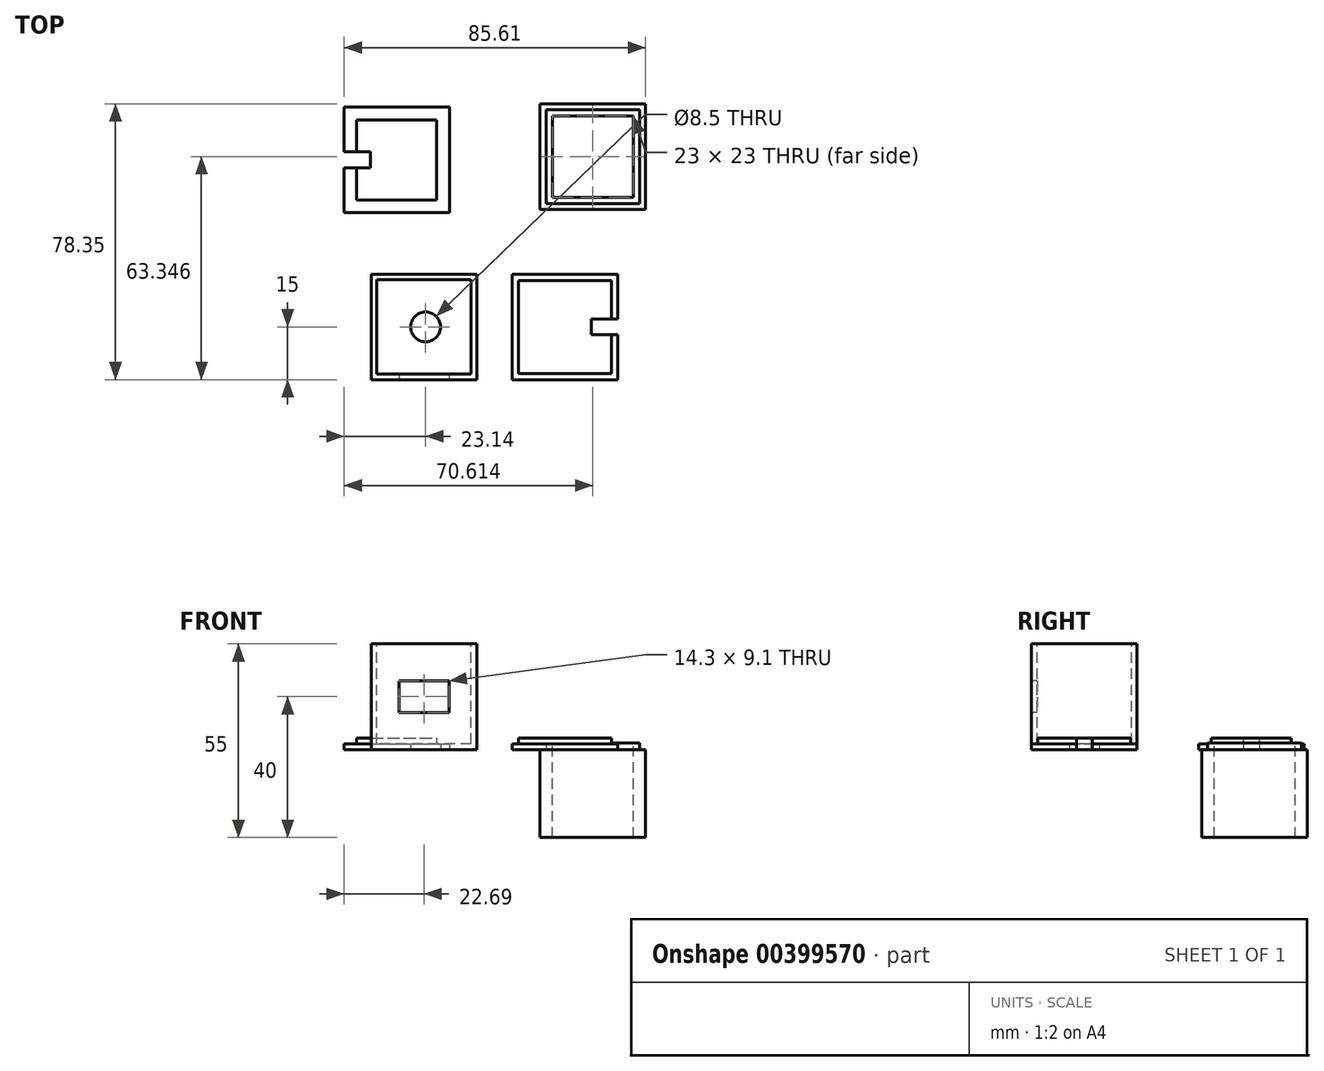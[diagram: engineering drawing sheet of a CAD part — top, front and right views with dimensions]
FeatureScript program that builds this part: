
annotation { "Feature Type Name" : "Feature", "Feature Type Description" : "" }
export const myFeature = defineFeature(function(context is Context, id is Id, definition is map)
    precondition{}
    {
        {
            var Q0;
            Q0=qCreatedBy(makeId("Front.planeOp"),FACE);
            var sketch = newSketch(context, id + "F0", { "sketchPlane" : qUnion([Q0])});
            skLineSegment(sketch, "E0.bottom", {"start": v(0, 0) * mm, "end": v(-30, 0) * mm});
            skLineSegment(sketch, "E0.top", {"start": v(0, 30) * mm, "end": v(-30, 30) * mm});
            skLineSegment(sketch, "E0.left", {"start": v(0, 0) * mm, "end": v(0, 30) * mm});
            skLineSegment(sketch, "E0.right", {"start": v(-30, 0) * mm, "end": v(-30, 30) * mm});
            skSolve(sketch);
        }
        {
            var Q0;
            Q0=makeQuery(id+"F0.imprint","IMPRINT",FACE,{"disambiguationData":[TD([[makeQuery(id+"F0.imprint","IMPRINT",EDGE,{"derivedFrom":sQuery(id+"F0.wireOp",EDGE,"E0.bottom")}),-1.0]])]});
            extrude(context, id + "F1", {"entities" : qUnion([Q0]), "depth" : 30 * mm});
        }
        {
            var Q0;
            Q0=makeQuery(id+"F1.opExtrude","SWEPT_FACE",FACE,{"disambiguationData":[OSD([sQuery(id+"F0.wireOp",EDGE,"E0.top")])]});
            shell(context, id + "F2", {"entities" : qUnion([Q0]), "thickness" : 1.6 * mm});
        }
        {
            var Q0;
            Q0=makeQuery(id+"F1.opExtrude","CAP_FACE",FACE,{"disambiguationData":[OSD([sQuery(id+"F0.wireOp",EDGE,"E0.bottom"),sQuery(id+"F0.wireOp",EDGE,"E0.top"),sQuery(id+"F0.wireOp",EDGE,"E0.left"),sQuery(id+"F0.wireOp",EDGE,"E0.right")])],"isStart":false});
            var sketch = newSketch(context, id + "F3", { "sketchPlane" : qUnion([Q0])});
            skLineSegment(sketch, "E1.bottom", {"start": v(-22.15, 19.55) * mm, "end": v(-7.85, 19.55) * mm});
            skLineSegment(sketch, "E1.top", {"start": v(-22.15, 10.45) * mm, "end": v(-7.85, 10.45) * mm});
            skLineSegment(sketch, "E1.left", {"start": v(-22.15, 19.55) * mm, "end": v(-22.15, 10.45) * mm});
            skLineSegment(sketch, "E1.right", {"start": v(-7.85, 19.55) * mm, "end": v(-7.85, 10.45) * mm});
            skLineSegment(sketch, "E2", {"start": v(-15, 30) * mm, "end": v(-15, 0) * mm, "construction": true});
            skLineSegment(sketch, "E3", {"start": v(-15, 19.55) * mm, "end": v(-15, 10.45) * mm, "construction": true});
            skLineSegment(sketch, "E4", {"start": v(0, 15) * mm, "end": v(-30, 15) * mm, "construction": true});
            skLineSegment(sketch, "E5", {"start": v(-22.15, 15) * mm, "end": v(-7.85, 15) * mm, "construction": true});
            skSolve(sketch);
        }
        {
            var Q0;
            Q0=makeQuery(id+"F3.imprint","IMPRINT",FACE,{"disambiguationData":[TD([[makeQuery(id+"F3.imprint","IMPRINT",EDGE,{"derivedFrom":sQuery(id+"F3.wireOp",EDGE,"E1.bottom")}),-1.0]])]});
            extrude(context, id + "F4", {"entities" : qUnion([Q0]), "operationType" : NewBodyOperationType.REMOVE, "oppositeDirection" : true, "depth" : 1.6 * mm});
        }
        {
            var Q0;
            Q0=makeQuery(id+"F1.opExtrude","SWEPT_FACE",FACE,{"disambiguationData":[OSD([sQuery(id+"F0.wireOp",EDGE,"E0.bottom")])]});
            var sketch = newSketch(context, id + "F5", { "sketchPlane" : qUnion([Q0])});
            skLineSegment(sketch, "E6", {"start": v(-30, 15) * mm, "end": v(0, 15) * mm, "construction": true});
            skCircle(sketch, "E7", {"center": v(-14.55, 15) * mm, "radius": 4.25 * mm});
            skSolve(sketch);
        }
        {
            var Q0;
            Q0=makeQuery(id+"F5.imprint","IMPRINT",FACE,{"disambiguationData":[TD([[makeQuery(id+"F5.imprint","IMPRINT",EDGE,{"derivedFrom":sQuery(id+"F5.wireOp",EDGE,"E7")}),1.0]])]});
            extrude(context, id + "F6", {"entities" : qUnion([Q0]), "operationType" : NewBodyOperationType.REMOVE, "oppositeDirection" : true, "depth" : 1.6 * mm});
        }
        {
            var Q0;
            Q0=qCreatedBy(makeId("Top.planeOp"),FACE);
            var sketch = newSketch(context, id + "F7", { "sketchPlane" : qUnion([Q0])});
            skLineSegment(sketch, "E8.bottom", {"start": v(10.04, 0) * mm, "end": v(40.04, 0) * mm});
            skLineSegment(sketch, "E8.top", {"start": v(10.04, -30) * mm, "end": v(40.04, -30) * mm});
            skLineSegment(sketch, "E8.left", {"start": v(10.04, 0) * mm, "end": v(10.04, -30) * mm});
            skLineSegment(sketch, "E8.right", {"start": v(40.04, 0) * mm, "end": v(40.04, -30) * mm});
            skLineSegment(sketch, "E9.bottom", {"start": v(11.84, -1.8) * mm, "end": v(38.24, -1.8) * mm});
            skLineSegment(sketch, "E9.top", {"start": v(11.84, -28.2) * mm, "end": v(38.24, -28.2) * mm});
            skLineSegment(sketch, "E9.left", {"start": v(11.84, -1.8) * mm, "end": v(11.84, -28.2) * mm});
            skLineSegment(sketch, "E9.right", {"start": v(38.24, -1.8) * mm, "end": v(38.24, -28.2) * mm});
            skLineSegment(sketch, "E10", {"start": v(25.04, 0) * mm, "end": v(25.04, -30) * mm, "construction": true});
            skLineSegment(sketch, "E11", {"start": v(25.04, -1.8) * mm, "end": v(25.04, -28.2) * mm});
            skLineSegment(sketch, "E12", {"start": v(40.04, -15) * mm, "end": v(10.04, -15) * mm, "construction": true});
            skSolve(sketch);
        }
        {
            var Q0;
            Q0=makeQuery(id+"F7.imprint","IMPRINT",FACE,{"disambiguationData":[TD([[makeQuery(id+"F7.imprint","IMPRINT",EDGE,{"derivedFrom":sQuery(id+"F7.wireOp",EDGE,"E8.bottom")}),-1.0]])]});
            var Q1;
            {var subQ0=sQuery(id+"F7.wireOp",EDGE,"E9.left");Q1=makeQuery(id+"F7.imprint","IMPRINT",FACE,{"disambiguationData":[TD([[makeQuery(id+"F7.imprint","IMPRINT",EDGE,{"derivedFrom":subQ0}),1.0]])]});}
            var Q2;
            {var subQ0=sQuery(id+"F7.wireOp",EDGE,"E9.right");Q2=makeQuery(id+"F7.imprint","IMPRINT",FACE,{"disambiguationData":[TD([[makeQuery(id+"F7.imprint","IMPRINT",EDGE,{"derivedFrom":subQ0}),-1.0]])]});}
            extrude(context, id + "F8", {"entities" : qUnion([Q0, Q1, Q2]), "operationType" : NewBodyOperationType.ADD, "depth" : 1.6 * mm});
        }
        {
            var Q0;
            Q0=makeQuery(id+"F8.opExtrude","CAP_FACE",FACE,{"disambiguationData":[OSD([sQuery(id+"F7.wireOp",EDGE,"E8.bottom"),sQuery(id+"F7.wireOp",EDGE,"E8.top"),sQuery(id+"F7.wireOp",EDGE,"E8.left"),sQuery(id+"F7.wireOp",EDGE,"E8.right")])],"isStart":false});
            var sketch = newSketch(context, id + "F9", { "sketchPlane" : qUnion([Q0])});
            skLineSegment(sketch, "E13.0", {"start": v(11.84, -1.8) * mm, "end": v(38.24, -1.8) * mm});
            skLineSegment(sketch, "E14.0", {"start": v(11.84, -1.8) * mm, "end": v(11.84, -28.2) * mm});
            skLineSegment(sketch, "E15.0", {"start": v(11.84, -28.2) * mm, "end": v(38.24, -28.2) * mm});
            skLineSegment(sketch, "E16.0", {"start": v(38.24, -1.8) * mm, "end": v(38.24, -28.2) * mm});
            skSolve(sketch);
        }
        {
            var Q0;
            Q0=makeQuery(id+"F9.imprint","IMPRINT",FACE,{"disambiguationData":[TD([[makeQuery(id+"F9.imprint","IMPRINT",EDGE,{"derivedFrom":sQuery(id+"F9.wireOp",EDGE,"E13.0")}),-1.0]])]});
            extrude(context, id + "F10", {"entities" : qUnion([Q0]), "operationType" : NewBodyOperationType.ADD, "depth" : 1.6 * mm});
        }
        {
            var Q0;
            Q0=makeQuery(id+"F7.imprint","IMPRINT",FACE,{"disambiguationData":[TD([[makeQuery(id+"F7.imprint","IMPRINT",EDGE,{"derivedFrom":sQuery(id+"F7.wireOp",EDGE,"E8.bottom")}),-1.0]])]});
            var sketch = newSketch(context, id + "F11", { "sketchPlane" : qUnion([Q0])});
            skLineSegment(sketch, "E17.bottom", {"start": v(32.54, -17.25) * mm, "end": v(40.04, -17.25) * mm});
            skLineSegment(sketch, "E17.top", {"start": v(32.54, -12.75) * mm, "end": v(40.04, -12.75) * mm});
            skLineSegment(sketch, "E17.left", {"start": v(32.54, -17.25) * mm, "end": v(32.54, -12.75) * mm});
            skLineSegment(sketch, "E17.right", {"start": v(40.04, -17.25) * mm, "end": v(40.04, -12.75) * mm});
            skLineSegment(sketch, "E18", {"start": v(32.54, -15) * mm, "end": v(40.04, -15) * mm, "construction": true});
            skSolve(sketch);
        }
        {
            var Q0;
            Q0 = qSketchRegion(id + "F11", true);
            extrude(context, id + "F12", {"entities" : qUnion([Q0]), "operationType" : NewBodyOperationType.REMOVE, "endBound" : BoundingType.THROUGH_ALL, "depth" : 25 * mm});
        }
        {
            var Q0;
            Q0=qCreatedBy(makeId("Top.planeOp"),FACE);
            var sketch = newSketch(context, id + "F13", { "sketchPlane" : qUnion([Q0])});
            skLineSegment(sketch, "E19.bottom", {"start": v(17.92, 48.35) * mm, "end": v(47.92, 48.35) * mm});
            skLineSegment(sketch, "E19.top", {"start": v(17.92, 18.35) * mm, "end": v(47.92, 18.35) * mm});
            skLineSegment(sketch, "E19.left", {"start": v(17.92, 48.35) * mm, "end": v(17.92, 18.35) * mm});
            skLineSegment(sketch, "E19.right", {"start": v(47.92, 48.35) * mm, "end": v(47.92, 18.35) * mm});
            skSolve(sketch);
        }
        {
            var Q0;
            Q0=makeQuery(id+"F13.imprint","IMPRINT",FACE,{"disambiguationData":[TD([[makeQuery(id+"F13.imprint","IMPRINT",EDGE,{"derivedFrom":sQuery(id+"F13.wireOp",EDGE,"E19.bottom")}),-1.0]])]});
            extrude(context, id + "F14", {"entities" : qUnion([Q0]), "oppositeDirection" : true, "depth" : 25 * mm});
        }
        {
            var Q0;
            Q0=makeQuery(id+"F14.opExtrude","CAP_FACE",FACE,{"disambiguationData":[OSD([sQuery(id+"F13.wireOp",EDGE,"E19.bottom"),sQuery(id+"F13.wireOp",EDGE,"E19.top"),sQuery(id+"F13.wireOp",EDGE,"E19.left"),sQuery(id+"F13.wireOp",EDGE,"E19.right")])],"isStart":true});
            var sketch = newSketch(context, id + "F15", { "sketchPlane" : qUnion([Q0])});
            skLineSegment(sketch, "E20.bottom", {"start": v(19.62, 46.65) * mm, "end": v(46.22, 46.65) * mm});
            skLineSegment(sketch, "E20.top", {"start": v(19.62, 20.05) * mm, "end": v(46.22, 20.05) * mm});
            skLineSegment(sketch, "E20.left", {"start": v(19.62, 46.65) * mm, "end": v(19.62, 20.05) * mm});
            skLineSegment(sketch, "E20.right", {"start": v(46.22, 46.65) * mm, "end": v(46.22, 20.05) * mm});
            skSolve(sketch);
        }
        {
            var Q0;
            Q0=makeQuery(id+"F15.imprint","IMPRINT",FACE,{"disambiguationData":[TD([[makeQuery(id+"F15.imprint","IMPRINT",EDGE,{"derivedFrom":sQuery(id+"F15.wireOp",EDGE,"E20.bottom")}),-1.0]])]});
            extrude(context, id + "F16", {"entities" : qUnion([Q0]), "operationType" : NewBodyOperationType.ADD, "depth" : 1.8 * mm});
        }
        {
            var Q0;
            Q0=makeQuery(id+"F16.opExtrude","CAP_FACE",FACE,{"disambiguationData":[OSD([sQuery(id+"F15.wireOp",EDGE,"E20.bottom"),sQuery(id+"F15.wireOp",EDGE,"E20.top"),sQuery(id+"F15.wireOp",EDGE,"E20.left"),sQuery(id+"F15.wireOp",EDGE,"E20.right")])],"isStart":false});
            var sketch = newSketch(context, id + "F17", { "sketchPlane" : qUnion([Q0])});
            skLineSegment(sketch, "E21.bottom", {"start": v(21.42, 44.85) * mm, "end": v(44.42, 44.85) * mm});
            skLineSegment(sketch, "E21.top", {"start": v(21.42, 21.85) * mm, "end": v(44.42, 21.85) * mm});
            skLineSegment(sketch, "E21.left", {"start": v(21.42, 44.85) * mm, "end": v(21.42, 21.85) * mm});
            skLineSegment(sketch, "E21.right", {"start": v(44.42, 44.85) * mm, "end": v(44.42, 21.85) * mm});
            skSolve(sketch);
        }
        {
            var Q0;
            Q0=makeQuery(id+"F17.imprint","IMPRINT",FACE,{"disambiguationData":[TD([[makeQuery(id+"F17.imprint","IMPRINT",EDGE,{"derivedFrom":sQuery(id+"F17.wireOp",EDGE,"E21.bottom")}),-1.0]])]});
            extrude(context, id + "F18", {"entities" : qUnion([Q0]), "operationType" : NewBodyOperationType.REMOVE, "endBound" : BoundingType.THROUGH_ALL, "oppositeDirection" : true, "depth" : 25 * mm});
        }
        {
            var Q0;
            Q0=qCreatedBy(makeId("Top.planeOp"),FACE);
            var sketch = newSketch(context, id + "F19", { "sketchPlane" : qUnion([Q0])});
            skLineSegment(sketch, "E22.bottom", {"start": v(-37.7, 47.46) * mm, "end": v(-7.7, 47.46) * mm});
            skLineSegment(sketch, "E22.top", {"start": v(-37.7, 17.46) * mm, "end": v(-7.7, 17.46) * mm});
            skLineSegment(sketch, "E22.left", {"start": v(-37.7, 47.46) * mm, "end": v(-37.7, 17.46) * mm});
            skLineSegment(sketch, "E22.right", {"start": v(-7.7, 47.46) * mm, "end": v(-7.7, 17.46) * mm});
            skSolve(sketch);
        }
        {
            var Q0;
            Q0=makeQuery(id+"F19.imprint","IMPRINT",FACE,{"disambiguationData":[TD([[makeQuery(id+"F19.imprint","IMPRINT",EDGE,{"derivedFrom":sQuery(id+"F19.wireOp",EDGE,"E22.bottom")}),-1.0]])]});
            extrude(context, id + "F20", {"entities" : qUnion([Q0]), "depth" : 1.6 * mm});
        }
        {
            var Q0;
            Q0=makeQuery(id+"F20.opExtrude","CAP_FACE",FACE,{"disambiguationData":[OSD([sQuery(id+"F19.wireOp",EDGE,"E22.bottom"),sQuery(id+"F19.wireOp",EDGE,"E22.top"),sQuery(id+"F19.wireOp",EDGE,"E22.left"),sQuery(id+"F19.wireOp",EDGE,"E22.right")])],"isStart":false});
            var sketch = newSketch(context, id + "F21", { "sketchPlane" : qUnion([Q0])});
            skLineSegment(sketch, "E23.bottom", {"start": v(-34.12, 43.78) * mm, "end": v(-11.37, 43.78) * mm});
            skLineSegment(sketch, "E23.top", {"start": v(-34.12, 21.03) * mm, "end": v(-11.37, 21.03) * mm});
            skLineSegment(sketch, "E23.left", {"start": v(-34.12, 43.78) * mm, "end": v(-34.12, 21.03) * mm});
            skLineSegment(sketch, "E23.right", {"start": v(-11.37, 43.78) * mm, "end": v(-11.37, 21.03) * mm});
            skSolve(sketch);
        }
        {
            var Q0;
            Q0=makeQuery(id+"F21.imprint","IMPRINT",FACE,{"disambiguationData":[TD([[makeQuery(id+"F21.imprint","IMPRINT",EDGE,{"derivedFrom":sQuery(id+"F21.wireOp",EDGE,"E23.bottom")}),-1.0]])]});
            extrude(context, id + "F22", {"entities" : qUnion([Q0]), "operationType" : NewBodyOperationType.ADD, "depth" : 1.6 * mm});
        }
        {
            var Q0;
            Q0=makeQuery(id+"F20.opExtrude","CAP_FACE",FACE,{"disambiguationData":[OSD([sQuery(id+"F19.wireOp",EDGE,"E22.bottom"),sQuery(id+"F19.wireOp",EDGE,"E22.top"),sQuery(id+"F19.wireOp",EDGE,"E22.left"),sQuery(id+"F19.wireOp",EDGE,"E22.right")])],"isStart":true});
            var sketch = newSketch(context, id + "F23", { "sketchPlane" : qUnion([Q0])});
            skLineSegment(sketch, "E24", {"start": v(-22.7, -17.46) * mm, "end": v(-22.7, -47.46) * mm, "construction": true});
            skLineSegment(sketch, "E25", {"start": v(-37.7, -32.46) * mm, "end": v(-7.7, -32.46) * mm, "construction": true});
            skLineSegment(sketch, "E26.bottom", {"start": v(-37.7, -34.76) * mm, "end": v(-30.2, -34.76) * mm});
            skLineSegment(sketch, "E26.top", {"start": v(-37.7, -30.16) * mm, "end": v(-30.2, -30.16) * mm});
            skLineSegment(sketch, "E26.left", {"start": v(-37.7, -34.76) * mm, "end": v(-37.7, -30.16) * mm});
            skLineSegment(sketch, "E26.right", {"start": v(-30.2, -34.76) * mm, "end": v(-30.2, -30.16) * mm});
            skSolve(sketch);
        }
        {
            var Q0;
            Q0=makeQuery(id+"F23.imprint","IMPRINT",FACE,{"disambiguationData":[TD([[makeQuery(id+"F23.imprint","IMPRINT",EDGE,{"derivedFrom":sQuery(id+"F23.wireOp",EDGE,"E26.bottom")}),1.0]])]});
            extrude(context, id + "F24", {"entities" : qUnion([Q0]), "operationType" : NewBodyOperationType.REMOVE, "endBound" : BoundingType.THROUGH_ALL, "oppositeDirection" : true, "depth" : 25 * mm});
        }
    });
